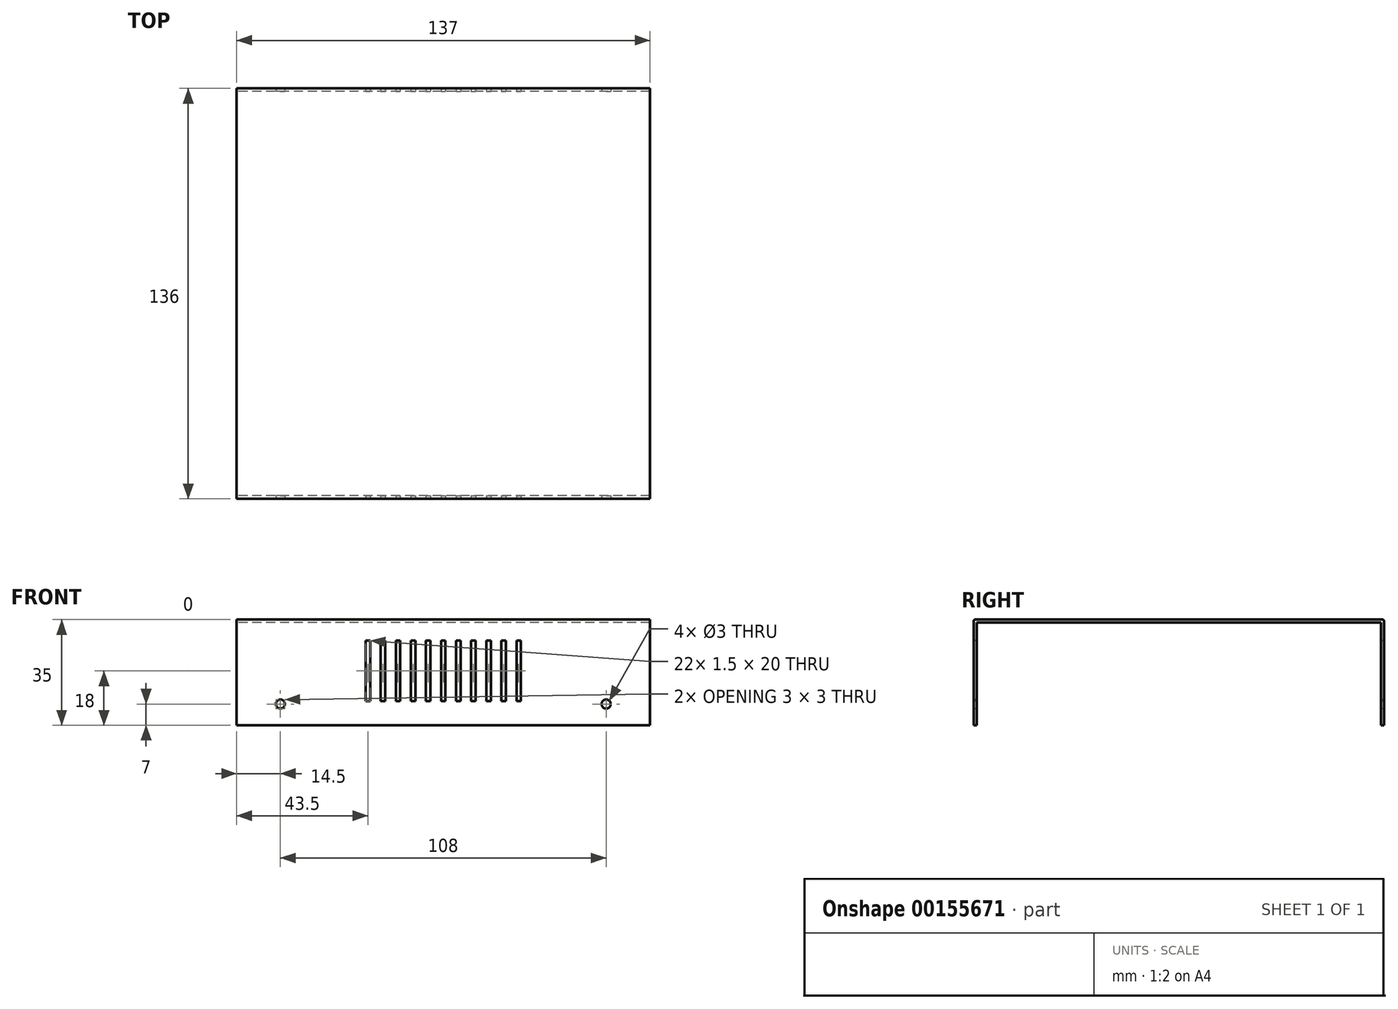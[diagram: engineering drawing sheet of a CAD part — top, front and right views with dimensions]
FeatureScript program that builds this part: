
annotation { "Feature Type Name" : "Feature", "Feature Type Description" : "" }
export const myFeature = defineFeature(function(context is Context, id is Id, definition is map)
    precondition{}
    {
        {
            var Q0;
            Q0=qCreatedBy(makeId("Top.planeOp"),FACE);
            var sketch = newSketch(context, id + "F0", { "sketchPlane" : qUnion([Q0])});
            skLineSegment(sketch, "E0.bottom", {"start": v(68.5, -67) * mm, "end": v(-68.5, -67) * mm});
            skLineSegment(sketch, "E0.top", {"start": v(68.5, 67) * mm, "end": v(-68.5, 67) * mm});
            skLineSegment(sketch, "E0.left", {"start": v(68.5, -67) * mm, "end": v(68.5, 67) * mm});
            skLineSegment(sketch, "E0.right", {"start": v(-68.5, -67) * mm, "end": v(-68.5, 67) * mm});
            skPoint(sketch, "E0.middle", {"position": v(0, 0) * mm});
            skSolve(sketch);
        }
        {
            var Q0;
            Q0 = qSketchRegion(id + "F0", true);
            extrude(context, id + "F1", {"entities" : qUnion([Q0]), "depth" : 1 * mm});
        }
        {
            var Q0;
            Q0=makeQuery(id+"F1.opExtrude","CAP_FACE",FACE,{"disambiguationData":[OSD([sQuery(id+"F0.wireOp",EDGE,"E0.bottom"),sQuery(id+"F0.wireOp",EDGE,"E0.top"),sQuery(id+"F0.wireOp",EDGE,"E0.left"),sQuery(id+"F0.wireOp",EDGE,"E0.right")])],"isStart":false});
            var sketch = newSketch(context, id + "F2", { "sketchPlane" : qUnion([Q0])});
            skLineSegment(sketch, "E1.bottom", {"start": v(-68.5, -67) * mm, "end": v(68.5, -67) * mm});
            skLineSegment(sketch, "E1.top", {"start": v(-68.5, -68) * mm, "end": v(68.5, -68) * mm});
            skLineSegment(sketch, "E1.left", {"start": v(-68.5, -67) * mm, "end": v(-68.5, -68) * mm});
            skLineSegment(sketch, "E1.right", {"start": v(68.5, -67) * mm, "end": v(68.5, -68) * mm});
            skLineSegment(sketch, "E2.bottom", {"start": v(-68.5, 67) * mm, "end": v(68.5, 67) * mm});
            skLineSegment(sketch, "E2.top", {"start": v(-68.5, 68) * mm, "end": v(68.5, 68) * mm});
            skLineSegment(sketch, "E2.left", {"start": v(-68.5, 67) * mm, "end": v(-68.5, 68) * mm});
            skLineSegment(sketch, "E2.right", {"start": v(68.5, 67) * mm, "end": v(68.5, 68) * mm});
            skSolve(sketch);
        }
        {
            var Q0;
            Q0 = qSketchRegion(id + "F2", true);
            extrude(context, id + "F3", {"entities" : qUnion([Q0]), "operationType" : NewBodyOperationType.ADD, "oppositeDirection" : true, "depth" : 35 * mm});
        }
        {
            var Q0;
            Q0=makeQuery(id+"F3.opExtrude","SWEPT_FACE",FACE,{"disambiguationData":[OSD([sQuery(id+"F2.wireOp",EDGE,"E1.top")])]});
            var sketch = newSketch(context, id + "F4", { "sketchPlane" : qUnion([Q0])});
            skCircle(sketch, "E3", {"center": v(-54, -27) * mm, "radius": 1.5 * mm});
            skCircle(sketch, "E4", {"center": v(54, -27) * mm, "radius": 1.5 * mm});
            skLineSegment(sketch, "E5.bottom", {"start": v(-24.25, -26) * mm, "end": v(-25.75, -26) * mm});
            skLineSegment(sketch, "E5.top", {"start": v(-24.25, -6) * mm, "end": v(-25.75, -6) * mm});
            skLineSegment(sketch, "E5.left", {"start": v(-24.25, -26) * mm, "end": v(-24.25, -6) * mm});
            skLineSegment(sketch, "E5.right", {"start": v(-25.75, -26) * mm, "end": v(-25.75, -6) * mm});
            skPoint(sketch, "E5.middle", {"position": v(-25, -16) * mm});
            skPoint(sketch, "E6.1.0.0", {"position": v(-20, -16) * mm});
            skLineSegment(sketch, "E6.1.0.1", {"start": v(-19.25, -26) * mm, "end": v(-19.25, -6) * mm});
            skLineSegment(sketch, "E6.1.0.2", {"start": v(-20.75, -26) * mm, "end": v(-20.75, -6) * mm});
            skLineSegment(sketch, "E6.1.0.3", {"start": v(-19.25, -26) * mm, "end": v(-20.75, -26) * mm});
            skLineSegment(sketch, "E6.1.0.4", {"start": v(-19.25, -6) * mm, "end": v(-20.75, -6) * mm});
            skPoint(sketch, "E6.2.0.0", {"position": v(-15, -16) * mm});
            skLineSegment(sketch, "E6.2.0.1", {"start": v(-14.25, -26) * mm, "end": v(-14.25, -6) * mm});
            skLineSegment(sketch, "E6.2.0.2", {"start": v(-15.75, -26) * mm, "end": v(-15.75, -6) * mm});
            skLineSegment(sketch, "E6.2.0.3", {"start": v(-14.25, -26) * mm, "end": v(-15.75, -26) * mm});
            skLineSegment(sketch, "E6.2.0.4", {"start": v(-14.25, -6) * mm, "end": v(-15.75, -6) * mm});
            skPoint(sketch, "E6.3.0.0", {"position": v(-10, -16) * mm});
            skLineSegment(sketch, "E6.3.0.1", {"start": v(-9.25, -26) * mm, "end": v(-9.25, -6) * mm});
            skLineSegment(sketch, "E6.3.0.2", {"start": v(-10.75, -26) * mm, "end": v(-10.75, -6) * mm});
            skLineSegment(sketch, "E6.3.0.3", {"start": v(-9.25, -26) * mm, "end": v(-10.75, -26) * mm});
            skLineSegment(sketch, "E6.3.0.4", {"start": v(-9.25, -6) * mm, "end": v(-10.75, -6) * mm});
            skPoint(sketch, "E6.4.0.0", {"position": v(-5, -16) * mm});
            skLineSegment(sketch, "E6.4.0.1", {"start": v(-4.25, -26) * mm, "end": v(-4.25, -6) * mm});
            skLineSegment(sketch, "E6.4.0.2", {"start": v(-5.75, -26) * mm, "end": v(-5.75, -6) * mm});
            skLineSegment(sketch, "E6.4.0.3", {"start": v(-4.25, -26) * mm, "end": v(-5.75, -26) * mm});
            skLineSegment(sketch, "E6.4.0.4", {"start": v(-4.25, -6) * mm, "end": v(-5.75, -6) * mm});
            skPoint(sketch, "E6.5.0.0", {"position": v(0, -16) * mm});
            skLineSegment(sketch, "E6.5.0.1", {"start": v(0.75, -26) * mm, "end": v(0.75, -6) * mm});
            skLineSegment(sketch, "E6.5.0.2", {"start": v(-0.75, -26) * mm, "end": v(-0.75, -6) * mm});
            skLineSegment(sketch, "E6.5.0.3", {"start": v(0.75, -26) * mm, "end": v(-0.75, -26) * mm});
            skLineSegment(sketch, "E6.5.0.4", {"start": v(0.75, -6) * mm, "end": v(-0.75, -6) * mm});
            skLineSegment(sketch, "E6.direction1", {"start": v(-25.75, -26) * mm, "end": v(-20.75, -26) * mm, "construction": true});
            skPoint(sketch, "E7.0.6.0", {"position": v(5, -16) * mm});
            skLineSegment(sketch, "E7.1.6.0", {"start": v(5.75, -26) * mm, "end": v(5.75, -6) * mm});
            skLineSegment(sketch, "E7.4.6.0", {"start": v(4.25, -26) * mm, "end": v(4.25, -6) * mm});
            skLineSegment(sketch, "E7.7.6.0", {"start": v(5.75, -26) * mm, "end": v(4.25, -26) * mm});
            skLineSegment(sketch, "E7.10.6.0", {"start": v(5.75, -6) * mm, "end": v(4.25, -6) * mm});
            skPoint(sketch, "E7.0.7.0", {"position": v(10, -16) * mm});
            skLineSegment(sketch, "E7.1.7.0", {"start": v(10.75, -26) * mm, "end": v(10.75, -6) * mm});
            skLineSegment(sketch, "E7.4.7.0", {"start": v(9.25, -26) * mm, "end": v(9.25, -6) * mm});
            skLineSegment(sketch, "E7.7.7.0", {"start": v(10.75, -26) * mm, "end": v(9.25, -26) * mm});
            skLineSegment(sketch, "E7.10.7.0", {"start": v(10.75, -6) * mm, "end": v(9.25, -6) * mm});
            skPoint(sketch, "E8.0.8.0", {"position": v(15, -16) * mm});
            skLineSegment(sketch, "E8.1.8.0", {"start": v(15.75, -26) * mm, "end": v(15.75, -6) * mm});
            skLineSegment(sketch, "E8.4.8.0", {"start": v(14.25, -26) * mm, "end": v(14.25, -6) * mm});
            skLineSegment(sketch, "E8.7.8.0", {"start": v(15.75, -26) * mm, "end": v(14.25, -26) * mm});
            skLineSegment(sketch, "E8.10.8.0", {"start": v(15.75, -6) * mm, "end": v(14.25, -6) * mm});
            skPoint(sketch, "E8.0.9.0", {"position": v(20, -16) * mm});
            skLineSegment(sketch, "E8.1.9.0", {"start": v(20.75, -26) * mm, "end": v(20.75, -6) * mm});
            skLineSegment(sketch, "E8.4.9.0", {"start": v(19.25, -26) * mm, "end": v(19.25, -6) * mm});
            skLineSegment(sketch, "E8.7.9.0", {"start": v(20.75, -26) * mm, "end": v(19.25, -26) * mm});
            skLineSegment(sketch, "E8.10.9.0", {"start": v(20.75, -6) * mm, "end": v(19.25, -6) * mm});
            skPoint(sketch, "E8.0.10.0", {"position": v(25, -16) * mm});
            skLineSegment(sketch, "E8.1.10.0", {"start": v(25.75, -26) * mm, "end": v(25.75, -6) * mm});
            skLineSegment(sketch, "E8.4.10.0", {"start": v(24.25, -26) * mm, "end": v(24.25, -6) * mm});
            skLineSegment(sketch, "E8.7.10.0", {"start": v(25.75, -26) * mm, "end": v(24.25, -26) * mm});
            skLineSegment(sketch, "E8.10.10.0", {"start": v(25.75, -6) * mm, "end": v(24.25, -6) * mm});
            skSolve(sketch);
        }
        {
            var Q0;
            Q0 = qSketchRegion(id + "F4", true);
            extrude(context, id + "F5", {"entities" : qUnion([Q0]), "operationType" : NewBodyOperationType.REMOVE, "endBound" : BoundingType.THROUGH_ALL, "oppositeDirection" : true, "depth" : 25 * mm});
        }
        {
            var Q0;
            Q0=makeQuery(id+"F3.opExtrude","CAP_EDGE",EDGE,{"disambiguationData":[OSD([sQuery(id+"F2.wireOp",EDGE,"E1.top")])],"isStart":true});
            var Q1;
            Q1=makeQuery(id+"F3.opExtrude","CAP_EDGE",EDGE,{"disambiguationData":[OSD([sQuery(id+"F2.wireOp",EDGE,"E2.top")])],"isStart":true});
            var Q2;
            Q2=makeQuery(id+"F1.opExtrude","CAP_EDGE",EDGE,{"disambiguationData":[OSD([sQuery(id+"F0.wireOp",EDGE,"E0.bottom")])],"isStart":true});
            var Q3;
            Q3=makeQuery(id+"F1.opExtrude","CAP_EDGE",EDGE,{"disambiguationData":[OSD([sQuery(id+"F0.wireOp",EDGE,"E0.top")])],"isStart":true});
            fillet(context, id + "F6", {"entities" : qUnion([Q0, Q1, Q2, Q3]), "radius" : 0.5 * mm, "tangentPropagation" : true, "allowEdgeOverflow" : false});
        }
    });
